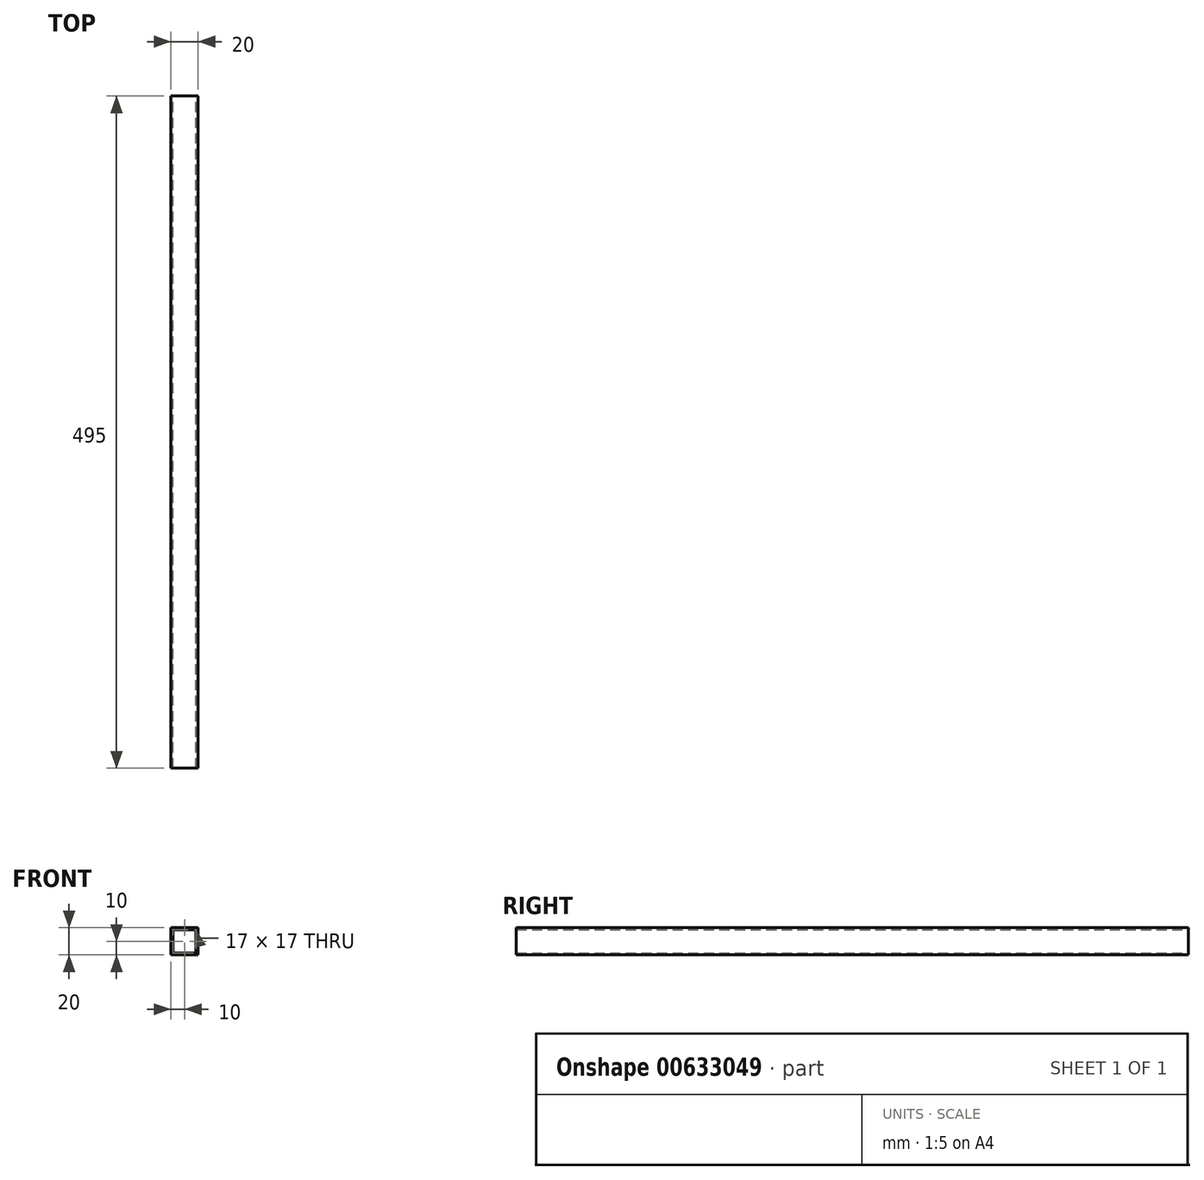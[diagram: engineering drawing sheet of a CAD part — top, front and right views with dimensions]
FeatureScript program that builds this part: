
annotation { "Feature Type Name" : "Feature", "Feature Type Description" : "" }
export const myFeature = defineFeature(function(context is Context, id is Id, definition is map)
    precondition{}
    {
        {
            var Q0;
            Q0=qCreatedBy(makeId("Front.planeOp"),FACE);
            var sketch = newSketch(context, id + "F0", { "sketchPlane" : qUnion([Q0])});
            skLineSegment(sketch, "E0.bottom", {"start": v(0, 0) * mm, "end": v(20, 0) * mm});
            skLineSegment(sketch, "E0.top", {"start": v(0, -20) * mm, "end": v(20, -20) * mm});
            skLineSegment(sketch, "E0.left", {"start": v(0, 0) * mm, "end": v(0, -20) * mm});
            skLineSegment(sketch, "E0.right", {"start": v(20, 0) * mm, "end": v(20, -20) * mm});
            skLineSegment(sketch, "E1.0", {"start": v(1.5, -1.5) * mm, "end": v(18.5, -1.5) * mm});
            skLineSegment(sketch, "E1.1", {"start": v(1.5, -1.5) * mm, "end": v(1.5, -18.5) * mm});
            skLineSegment(sketch, "E1.2", {"start": v(1.5, -18.5) * mm, "end": v(18.5, -18.5) * mm});
            skLineSegment(sketch, "E1.3", {"start": v(18.5, -1.5) * mm, "end": v(18.5, -18.5) * mm});
            skSolve(sketch);
        }
        {
            var Q0;
            Q0=makeQuery(id+"F0.imprint","IMPRINT",FACE,{"disambiguationData":[TD([[makeQuery(id+"F0.imprint","IMPRINT",EDGE,{"derivedFrom":sQuery(id+"F0.wireOp",EDGE,"E0.bottom")}),-1.0]])]});
            extrude(context, id + "F1", {"entities" : qUnion([Q0]), "depth" : 495 * mm, "offsetDistance" : 25 * mm});
        }
    });
